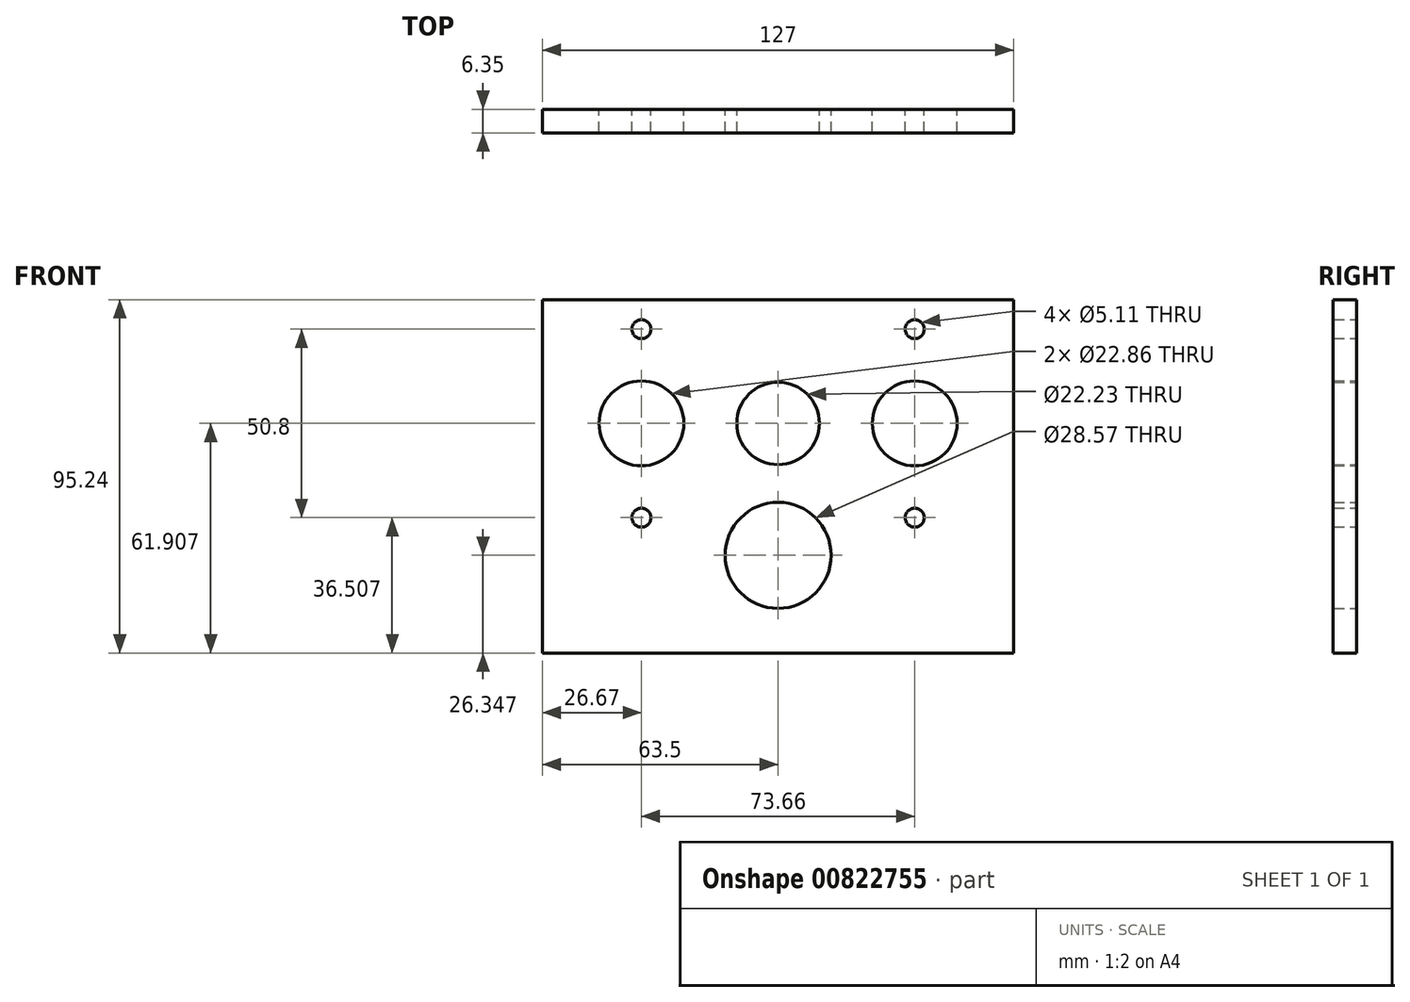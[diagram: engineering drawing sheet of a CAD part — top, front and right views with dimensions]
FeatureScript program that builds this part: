
annotation { "Feature Type Name" : "Feature", "Feature Type Description" : "" }
export const myFeature = defineFeature(function(context is Context, id is Id, definition is map)
    precondition{}
    {
        {
            var Q0;
            Q0=qCreatedBy(makeId("Front.planeOp"),FACE);
            var sketch = newSketch(context, id + "F0", { "sketchPlane" : qUnion([Q0])});
            skLineSegment(sketch, "E0.bottom", {"start": v(63.5, 47.63) * mm, "end": v(-63.5, 47.63) * mm});
            skLineSegment(sketch, "E0.top", {"start": v(63.5, -47.63) * mm, "end": v(-63.5, -47.63) * mm});
            skLineSegment(sketch, "E0.left", {"start": v(63.5, 47.63) * mm, "end": v(63.5, -47.63) * mm});
            skLineSegment(sketch, "E0.right", {"start": v(-63.5, 47.63) * mm, "end": v(-63.5, -47.63) * mm});
            skPoint(sketch, "E0.middle", {"position": v(0, 0) * mm});
            skCircle(sketch, "E1", {"center": v(0, -21.27) * mm, "radius": 21.59 * mm, "construction": true});
            skCircle(sketch, "E2", {"center": v(0, 14.29) * mm, "radius": 13.97 * mm, "construction": true});
            skCircle(sketch, "E3", {"center": v(0, 14.29) * mm, "radius": 27.94 * mm, "construction": true});
            skCircle(sketch, "E4", {"center": v(-36.83, 14.29) * mm, "radius": 8.9 * mm, "construction": true});
            skCircle(sketch, "E5", {"center": v(36.83, 14.29) * mm, "radius": 8.9 * mm, "construction": true});
            skLineSegment(sketch, "E6", {"start": v(0, 0) * mm, "end": v(0, 47.63) * mm, "construction": true});
            skCircle(sketch, "E7", {"center": v(-36.83, 14.29) * mm, "radius": 32 * mm, "construction": true});
            skCircle(sketch, "E8", {"center": v(36.83, 14.29) * mm, "radius": 32 * mm, "construction": true});
            skCircle(sketch, "E9", {"center": v(-36.83, 14.29) * mm, "radius": 25.4 * mm, "construction": true});
            skLineSegment(sketch, "E10", {"start": v(-36.83, 39.69) * mm, "end": v(-36.83, -11.11) * mm, "construction": true});
            skCircle(sketch, "E11", {"center": v(-36.83, 39.69) * mm, "radius": 2.55 * mm});
            skCircle(sketch, "E12", {"center": v(-36.83, -11.11) * mm, "radius": 2.55 * mm});
            skCircle(sketch, "E13.MirrorC", {"center": v(36.83, 39.69) * mm, "radius": 2.55 * mm});
            skCircle(sketch, "E14.MirrorC", {"center": v(36.83, -11.11) * mm, "radius": 2.55 * mm});
            skCircle(sketch, "E15", {"center": v(0, -21.27) * mm, "radius": 14.29 * mm});
            skCircle(sketch, "E16", {"center": v(0, 14.29) * mm, "radius": 11.11 * mm});
            skCircle(sketch, "E17", {"center": v(-36.83, 14.29) * mm, "radius": 11.43 * mm});
            skCircle(sketch, "E18.MirrorC", {"center": v(36.83, 14.29) * mm, "radius": 11.43 * mm});
            skSolve(sketch);
        }
        {
            var Q0;
            Q0=makeQuery(id+"F0.imprint","IMPRINT",FACE,{"disambiguationData":[TD([[makeQuery(id+"F0.imprint","IMPRINT",EDGE,{"derivedFrom":sQuery(id+"F0.wireOp",EDGE,"E0.bottom")}),1.0]])]});
            extrude(context, id + "F1", {"entities" : qUnion([Q0]), "depth" : 6.35 * mm, "offsetDistance" : 25.4 * mm});
        }
    });
